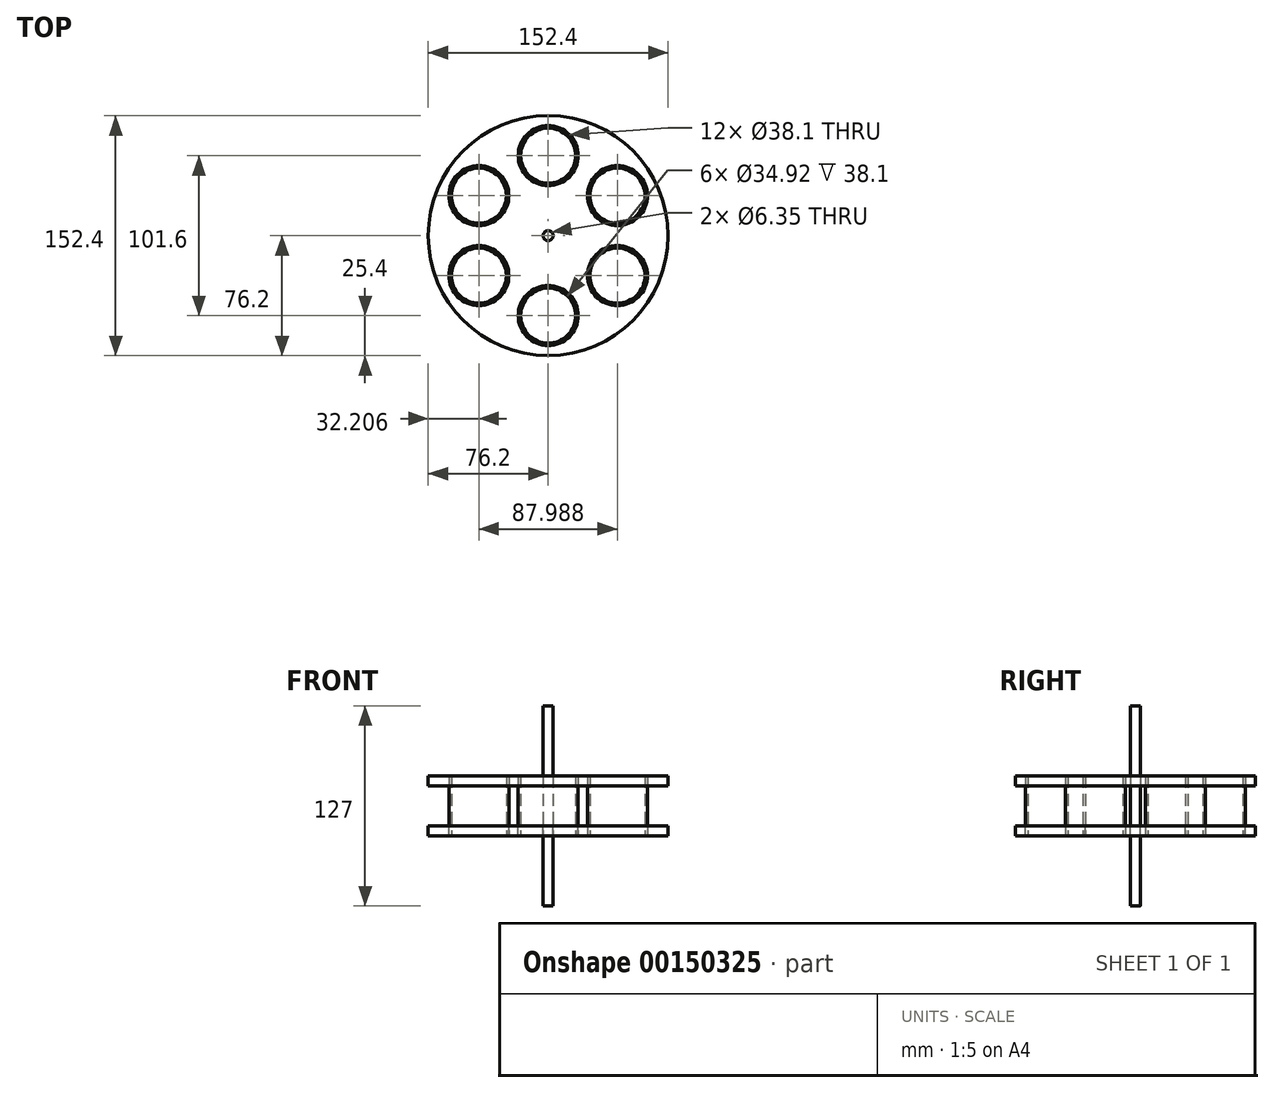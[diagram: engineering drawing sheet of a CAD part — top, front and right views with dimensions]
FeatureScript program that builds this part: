
annotation { "Feature Type Name" : "Feature", "Feature Type Description" : "" }
export const myFeature = defineFeature(function(context is Context, id is Id, definition is map)
    precondition{}
    {
        {
            var Q0;
            Q0=qCreatedBy(makeId("Top.planeOp"),FACE);
            var sketch = newSketch(context, id + "F0", { "sketchPlane" : qUnion([Q0])});
            skCircle(sketch, "E0", {"center": v(0, 0) * mm, "radius": 76.2 * mm});
            skSolve(sketch);
        }
        {
            var Q0;
            Q0 = qSketchRegion(id + "F0", true);
            extrude(context, id + "F1", {"entities" : qUnion([Q0]), "depth" : 6.35 * mm});
        }
        {
            var Q0;
            Q0=makeQuery(id+"F1.opExtrude","CAP_FACE",FACE,{"disambiguationData":[OSD([sQuery(id+"F0.wireOp",EDGE,"E0")])],"isStart":false});
            var sketch = newSketch(context, id + "F2", { "sketchPlane" : qUnion([Q0])});
            skLineSegment(sketch, "E1", {"start": v(0, 0) * mm, "end": v(0, 76.2) * mm, "construction": true});
            skLineSegment(sketch, "E2.1.0", {"start": v(0, 0) * mm, "end": v(-66, 38.1) * mm, "construction": true});
            skLineSegment(sketch, "E2.2.0", {"start": v(0, 0) * mm, "end": v(-66, -38.1) * mm, "construction": true});
            skLineSegment(sketch, "E2.3.0", {"start": v(0, 0) * mm, "end": v(0, -76.2) * mm, "construction": true});
            skLineSegment(sketch, "E2.4.0", {"start": v(0, 0) * mm, "end": v(66, -38.1) * mm, "construction": true});
            skLineSegment(sketch, "E2.5.0", {"start": v(0, 0) * mm, "end": v(66, 38.1) * mm, "construction": true});
            skPoint(sketch, "E2.center", {"position": v(0, 0) * mm});
            skCircle(sketch, "E3", {"center": v(0, 50.8) * mm, "radius": 19.05 * mm});
            skCircle(sketch, "E4.1.0", {"center": v(-44, 25.4) * mm, "radius": 19.05 * mm});
            skCircle(sketch, "E4.2.0", {"center": v(-44, -25.4) * mm, "radius": 19.05 * mm});
            skCircle(sketch, "E5.1.3.0", {"center": v(0, -50.8) * mm, "radius": 19.05 * mm});
            skCircle(sketch, "E5.1.4.0", {"center": v(44, -25.4) * mm, "radius": 19.05 * mm});
            skCircle(sketch, "E5.1.5.0", {"center": v(44, 25.4) * mm, "radius": 19.05 * mm});
            skCircle(sketch, "E6", {"center": v(0, 0) * mm, "radius": 3.18 * mm});
            skSolve(sketch);
        }
        {
            var Q0;
            Q0 = qSketchRegion(id + "F2", true);
            extrude(context, id + "F3", {"entities" : qUnion([Q0]), "operationType" : NewBodyOperationType.REMOVE, "endBound" : BoundingType.THROUGH_ALL, "oppositeDirection" : true, "depth" : 25.4 * mm});
        }
        {
            var Q0;
            Q0=makeQuery(id+"F1.opExtrude","CAP_FACE",FACE,{"disambiguationData":[OSD([sQuery(id+"F0.wireOp",EDGE,"E0")])],"isStart":true});
            var sketch = newSketch(context, id + "F4", { "sketchPlane" : qUnion([Q0])});
            skCircle(sketch, "E7", {"center": v(0, -50.8) * mm, "radius": 17.46 * mm});
            skCircle(sketch, "E8.0", {"center": v(0, -50.8) * mm, "radius": 19.05 * mm});
            skCircle(sketch, "E9.1.0", {"center": v(44, -25.4) * mm, "radius": 17.46 * mm});
            skCircle(sketch, "E9.1.1", {"center": v(44, -25.4) * mm, "radius": 19.05 * mm});
            skCircle(sketch, "E9.2.0", {"center": v(44, 25.4) * mm, "radius": 17.46 * mm});
            skCircle(sketch, "E9.2.1", {"center": v(44, 25.4) * mm, "radius": 19.05 * mm});
            skCircle(sketch, "E9.3.0", {"center": v(0, 50.8) * mm, "radius": 17.46 * mm});
            skCircle(sketch, "E9.3.1", {"center": v(0, 50.8) * mm, "radius": 19.05 * mm});
            skCircle(sketch, "E9.4.0", {"center": v(-44, 25.4) * mm, "radius": 17.46 * mm});
            skCircle(sketch, "E9.4.1", {"center": v(-44, 25.4) * mm, "radius": 19.05 * mm});
            skCircle(sketch, "E9.5.0", {"center": v(-44, -25.4) * mm, "radius": 17.46 * mm});
            skCircle(sketch, "E9.5.1", {"center": v(-44, -25.4) * mm, "radius": 19.05 * mm});
            skPoint(sketch, "E9.center", {"position": v(0, 0) * mm});
            skSolve(sketch);
        }
        {
            var Q0;
            Q0 = qSketchRegion(id + "F4", true);
            extrude(context, id + "F5", {"entities" : qUnion([Q0]), "oppositeDirection" : true, "depth" : 38.1 * mm});
        }
        {
            var Q0;
            Q0=makeQuery(id+"F1.opExtrude","CAP_FACE",FACE,{"disambiguationData":[OSD([sQuery(id+"F0.wireOp",EDGE,"E0")])],"isStart":false});
            cPlane(context, id + "F6", {"entities" : qUnion([Q0]), "cplaneType" : CPlaneType.OFFSET, "offset" : 12.7 * mm, "width" : 152.4 * mm, "height" : 152.4 * mm});
        }
        {
            var Q0;
            Q0=makeQuery(id+"F1.opExtrude","SWEPT_BODY",BODY,{"disambiguationData":[OSD([sQuery(id+"F0.wireOp",EDGE,"E0")])]});
            var Q1;
            Q1=qCreatedBy(id+"F6.planeOp",FACE);
            mirror(context, id + "F7", {"entities" : qUnion([Q0]), "mirrorPlane" : qUnion([Q1])});
        }
        {
            var Q0;
            Q0=qCreatedBy(id+"F6.planeOp",FACE);
            var sketch = newSketch(context, id + "F8", { "sketchPlane" : qUnion([Q0])});
            skCircle(sketch, "E10.0", {"center": v(0, 0) * mm, "radius": 3.18 * mm});
            skSolve(sketch);
        }
        {
            var Q0;
            Q0 = qSketchRegion(id + "F8", true);
            extrude(context, id + "F9", {"entities" : qUnion([Q0]), "depth" : 127 * mm, "symmetric" : true});
        }
    });
